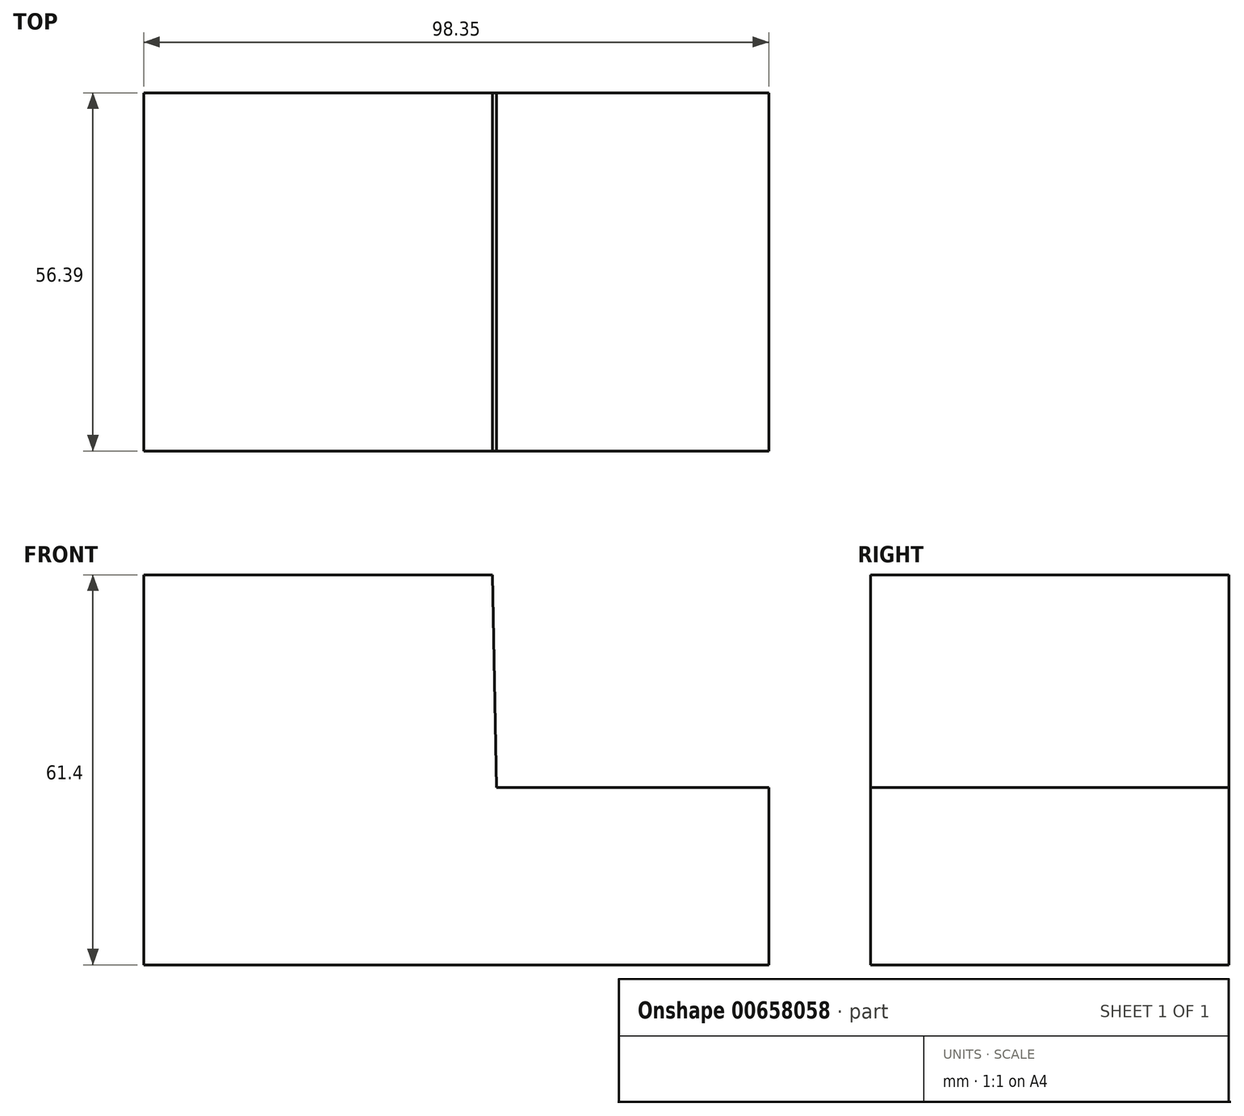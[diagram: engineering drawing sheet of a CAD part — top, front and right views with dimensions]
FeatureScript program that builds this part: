
annotation { "Feature Type Name" : "Feature", "Feature Type Description" : "" }
export const myFeature = defineFeature(function(context is Context, id is Id, definition is map)
    precondition{}
    {
        {
            var Q0;
            Q0=qCreatedBy(makeId("Front.planeOp"),FACE);
            var sketch = newSketch(context, id + "F0", { "sketchPlane" : qUnion([Q0])});
            skLineSegment(sketch, "E0", {"start": v(-4.8, -24.96) * mm, "end": v(49.46, -24.96) * mm});
            skLineSegment(sketch, "E1", {"start": v(49.46, -24.96) * mm, "end": v(49.46, -52.87) * mm});
            skLineSegment(sketch, "E2", {"start": v(49.46, -52.87) * mm, "end": v(-60.32, -52.87) * mm});
            skLineSegment(sketch, "E3", {"start": v(-60.32, -52.87) * mm, "end": v(-60.32, 8.53) * mm});
            skLineSegment(sketch, "E4", {"start": v(-60.32, 8.53) * mm, "end": v(-5.43, 8.53) * mm});
            skLineSegment(sketch, "E5", {"start": v(-5.43, 8.53) * mm, "end": v(-4.8, -24.96) * mm});
            skSolve(sketch);
        }
        {
            var Q0;
            Q0=makeQuery(id+"F0.imprint","IMPRINT",FACE,{"disambiguationData":[TD([[makeQuery(id+"F0.imprint","IMPRINT",EDGE,{"derivedFrom":sQuery(id+"F0.wireOp",EDGE,"E0")}),-1.0]])]});
            extrude(context, id + "F1", {"entities" : qUnion([Q0]), "depth" : 56.4 * mm, "offsetDistance" : 25.4 * mm});
        }
        {
            var Q0;
            Q0=makeQuery(id+"F1.opExtrude","SWEPT_FACE",FACE,{"disambiguationData":[OSD([sQuery(id+"F0.wireOp",EDGE,"E1")])]});
            extrude(context, id + "F2", {"entities" : qUnion([Q0]), "operationType" : NewBodyOperationType.REMOVE, "oppositeDirection" : true, "depth" : 11.43 * mm, "offsetDistance" : 25.4 * mm});
        }
    });
